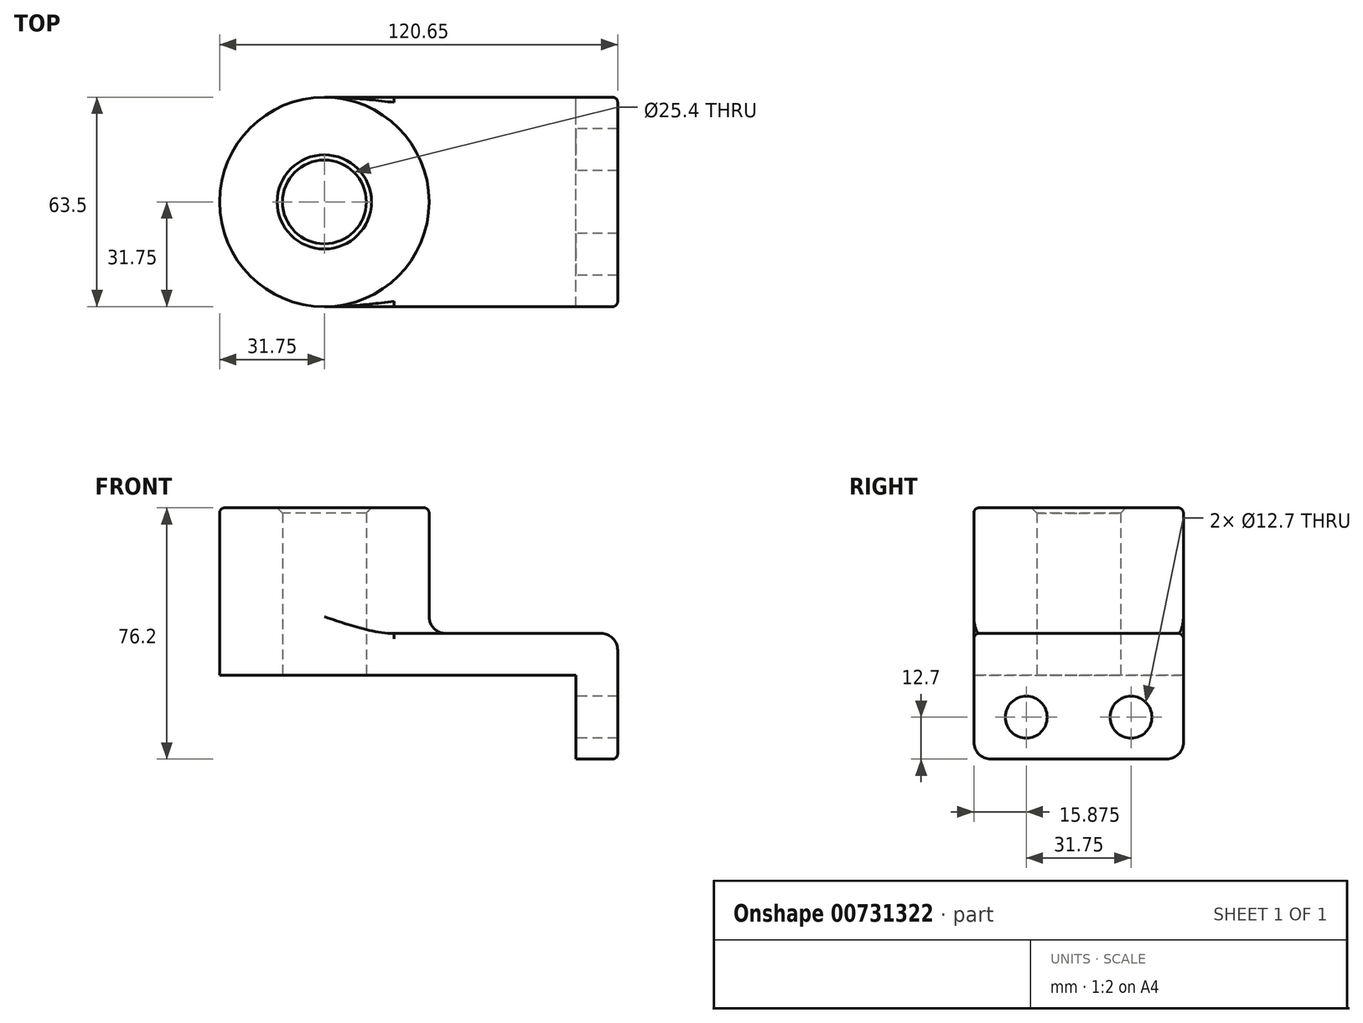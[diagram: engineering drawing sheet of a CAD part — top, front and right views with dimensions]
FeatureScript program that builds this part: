
annotation { "Feature Type Name" : "Feature", "Feature Type Description" : "" }
export const myFeature = defineFeature(function(context is Context, id is Id, definition is map)
    precondition{}
    {
        {
            var Q0;
            Q0=qCreatedBy(makeId("Top.planeOp"),FACE);
            var sketch = newSketch(context, id + "F0", { "sketchPlane" : qUnion([Q0])});
            skLineSegment(sketch, "E0.bottom", {"start": v(38.1, -31.75) * mm, "end": v(-38.1, -31.75) * mm});
            skLineSegment(sketch, "E0.top", {"start": v(38.1, 31.75) * mm, "end": v(-38.1, 31.75) * mm});
            skLineSegment(sketch, "E0.left", {"start": v(38.1, -31.75) * mm, "end": v(38.1, 31.75) * mm});
            skLineSegment(sketch, "E0.right", {"start": v(-38.1, -31.75) * mm, "end": v(-38.1, 31.75) * mm});
            skPoint(sketch, "E0.middle", {"position": v(0, 0) * mm});
            skCircle(sketch, "E1", {"center": v(-38.1, 0) * mm, "radius": 31.75 * mm});
            skCircle(sketch, "E2", {"center": v(-38.1, 0) * mm, "radius": 12.7 * mm});
            skSolve(sketch);
        }
        {
            var Q0;
            {var subQ1=sQuery(id+"F0.wireOp",EDGE,"E0.right");var subQ3=sQuery(id+"F0.wireOp",EDGE,"E2");var subQ4=makeQuery(id+"F0.imprint","INTERSECT",VERTEX,{"disambiguationData":[OD(0.0)],"derivedFrom":[subQ1,subQ3]});Q0=makeQuery(id+"F0.imprint","IMPRINT",FACE,{"disambiguationData":[TD([[makeQuery(id+"F0.imprint","IMPRINT",EDGE,{"disambiguationData":[TD([[subQ4,1.0]])],"derivedFrom":subQ3}),-1.0]])]});}
            var Q1;
            {var subQ1=sQuery(id+"F0.wireOp",EDGE,"E0.right");var subQ3=sQuery(id+"F0.wireOp",EDGE,"E2");var subQ4=makeQuery(id+"F0.imprint","INTERSECT",VERTEX,{"disambiguationData":[OD(0.0)],"derivedFrom":[subQ1,subQ3]});Q1=makeQuery(id+"F0.imprint","IMPRINT",FACE,{"disambiguationData":[TD([[makeQuery(id+"F0.imprint","IMPRINT",EDGE,{"disambiguationData":[TD([[subQ4,-1.0]])],"derivedFrom":subQ3}),-1.0]])]});}
            var Q2;
            {var subQ0=sQuery(id+"F0.wireOp",EDGE,"E0.bottom");Q2=makeQuery(id+"F0.imprint","IMPRINT",FACE,{"disambiguationData":[TD([[makeQuery(id+"F0.imprint","IMPRINT",EDGE,{"derivedFrom":subQ0}),-1.0]])]});}
            extrude(context, id + "F1", {"entities" : qUnion([Q0, Q1, Q2]), "depth" : 12.7 * mm, "offsetDistance" : 25.4 * mm});
        }
        {
            var Q0;
            {var subQ1=sQuery(id+"F0.wireOp",EDGE,"E0.right");var subQ3=sQuery(id+"F0.wireOp",EDGE,"E2");var subQ4=makeQuery(id+"F0.imprint","INTERSECT",VERTEX,{"disambiguationData":[OD(0.0)],"derivedFrom":[subQ1,subQ3]});Q0=makeQuery(id+"F0.imprint","IMPRINT",FACE,{"disambiguationData":[TD([[makeQuery(id+"F0.imprint","IMPRINT",EDGE,{"disambiguationData":[TD([[subQ4,-1.0]])],"derivedFrom":subQ3}),-1.0]])]});}
            var Q1;
            {var subQ1=sQuery(id+"F0.wireOp",EDGE,"E0.right");var subQ3=sQuery(id+"F0.wireOp",EDGE,"E2");var subQ4=makeQuery(id+"F0.imprint","INTERSECT",VERTEX,{"disambiguationData":[OD(0.0)],"derivedFrom":[subQ1,subQ3]});Q1=makeQuery(id+"F0.imprint","IMPRINT",FACE,{"disambiguationData":[TD([[makeQuery(id+"F0.imprint","IMPRINT",EDGE,{"disambiguationData":[TD([[subQ4,1.0]])],"derivedFrom":subQ3}),-1.0]])]});}
            extrude(context, id + "F2", {"entities" : qUnion([Q0, Q1]), "operationType" : NewBodyOperationType.ADD, "depth" : 50.8 * mm, "offsetDistance" : 25.4 * mm});
        }
        {
            var Q0;
            Q0=makeQuery(id+"F1.opExtrude","SWEPT_FACE",FACE,{"disambiguationData":[OSD([sQuery(id+"F0.wireOp",EDGE,"E0.left")])]});
            var sketch = newSketch(context, id + "F3", { "sketchPlane" : qUnion([Q0])});
            skLineSegment(sketch, "E3.bottom", {"start": v(-31.75, 12.7) * mm, "end": v(31.75, 12.7) * mm});
            skLineSegment(sketch, "E3.top", {"start": v(-31.75, -25.4) * mm, "end": v(31.75, -25.4) * mm});
            skLineSegment(sketch, "E3.left", {"start": v(-31.75, 12.7) * mm, "end": v(-31.75, -25.4) * mm});
            skLineSegment(sketch, "E3.right", {"start": v(31.75, 12.7) * mm, "end": v(31.75, -25.4) * mm});
            skLineSegment(sketch, "E4", {"start": v(0, 0) * mm, "end": v(0, -25.4) * mm});
            skCircle(sketch, "E5", {"center": v(-15.88, -12.7) * mm, "radius": 6.35 * mm});
            skPoint(sketch, "E5.centerSnap0", {"position": v(0, -12.7) * mm});
            skCircle(sketch, "E6.MirrorC", {"center": v(15.88, -12.7) * mm, "radius": 6.35 * mm});
            skSolve(sketch);
        }
        {
            var Q0;
            Q0 = qSketchRegion(id + "F3", true);
            extrude(context, id + "F4", {"entities" : qUnion([Q0]), "operationType" : NewBodyOperationType.ADD, "depth" : 12.7 * mm, "offsetDistance" : 25.4 * mm});
        }
        {
            var Q0;
            {var subQ0=sQuery(id+"F0.wireOp",EDGE,"E1");Q0=makeQuery(id+"F2.boolean.opBoolean","INTERSECT",EDGE,{"derivedFrom":[makeQuery(id+"F1.opExtrude","CAP_FACE",FACE,{"disambiguationData":[OSD([sQuery(id+"F0.wireOp",EDGE,"E0.bottom"),sQuery(id+"F0.wireOp",EDGE,"E0.top"),sQuery(id+"F0.wireOp",EDGE,"E0.left"),subQ0,sQuery(id+"F0.wireOp",EDGE,"E2")])],"isStart":false}),makeQuery(id+"F2.opExtrude","SWEPT_FACE",FACE,{"disambiguationData":[OSD([subQ0])]})]});}
            var Q1;
            Q1=makeQuery(id+"F4.opExtrude","CAP_EDGE",EDGE,{"disambiguationData":[OSD([sQuery(id+"F3.wireOp",EDGE,"E3.bottom")])],"isStart":false});
            var Q2;
            Q2=makeQuery(id+"F4.opExtrude","SWEPT_EDGE",EDGE,{"disambiguationData":[OSD([sQuery(id+"F3.wireOp",EDGE,"E3.top"),sQuery(id+"F3.wireOp",EDGE,"E3.left")])]});
            var Q3;
            Q3=makeQuery(id+"F4.opExtrude","SWEPT_EDGE",EDGE,{"disambiguationData":[OSD([sQuery(id+"F3.wireOp",EDGE,"E3.top"),sQuery(id+"F3.wireOp",EDGE,"E3.right")])]});
            var Q4;
            Q4=makeQuery(id+"F1.opExtrude","CAP_EDGE",EDGE,{"disambiguationData":[OSD([sQuery(id+"F0.wireOp",EDGE,"E0.left")])],"isStart":true});
            fillet(context, id + "F5", {"entities" : qUnion([Q0, Q1, Q2, Q3, Q4]), "radius" : 5.08 * mm, "tangentPropagation" : true, "allowEdgeOverflow" : false});
        }
        {
            var Q0;
            Q0=makeQuery(id+"F4.boolean.opBoolean","MERGE",EDGE,{"derivedFrom":[makeQuery(id+"F1.opExtrude","CAP_EDGE",EDGE,{"disambiguationData":[OSD([sQuery(id+"F0.wireOp",EDGE,"E0.bottom")])],"isStart":false}),makeQuery(id+"F4.opExtrude","SWEPT_EDGE",EDGE,{"disambiguationData":[OSD([sQuery(id+"F3.wireOp",EDGE,"E3.bottom"),sQuery(id+"F3.wireOp",EDGE,"E3.left")])]})]});
            var Q1;
            Q1=makeQuery(id+"F2.opExtrude","CAP_EDGE",EDGE,{"disambiguationData":[OSD([sQuery(id+"F0.wireOp",EDGE,"E1")])],"isStart":false});
            fillet(context, id + "F6", {"entities" : qUnion([Q0, Q1]), "radius" : 1.59 * mm, "tangentPropagation" : true, "allowEdgeOverflow" : false});
        }
        {
            var Q0;
            Q0=makeQuery(id+"F2.opExtrude","CAP_EDGE",EDGE,{"disambiguationData":[OSD([sQuery(id+"F0.wireOp",EDGE,"E2")])],"isStart":false});
            chamfer(context, id + "F7", {"entities" : qUnion([Q0]), "width" : 1.59 * mm, "tangentPropagation" : true});
        }
    });
